# Revit family: Dauphin-Bosse S4_Space Pod_V2
name_source: partatom
category: Casework
units: mm (PartAtom-declared; Revit-internal decimal feet)

## family parameters
Always vertical = Yes
Cut with Voids When Loaded = No
Room Calculation Point = No
Shared = No
Work Plane-Based = No

## types (4) — shared parameters
Dauphin Floor = Bosse_Fabric Divina Asphalt Grey
Dauphin_AC Console = Bosse_Door Metal Material
Dauphin_Glass = Bosse_Panel Glass Material
Dauphin_Handle = Bosse_Door Handle Material
Dauphin_Metal = Bosse_Panel Exterior Material
Dauphin_White = Bosse_Panel Exterior Material
Door Opening Width = 998 mm  [stored 3.27428 ft]
Door Width = 914 mm  [stored 2.99869 ft]
Front Panel Amounts = 3
Height = 2502 mm  [stored 8.20866 ft]
Manufacturer = Dauphin North America
Type Comments = Bosse Series 4

## per-type parameters (varying)
| type | Back Panel Amount | Depth | Description | Floor Width | Froor Depth | Light Visibility | Model | Side Panel Amounts | Width |
| Bosse S4 - Small | 3 | 2514 mm  [stored 8.24803 ft] | Bosse S4 Small PURE | 1996 mm  [stored 6.54856 ft] | 2358 mm  [stored 7.73622 ft] | No | BP4S_P85X99X99 | 3 | 2152 mm  [stored 7.06037 ft] |
| Bosse S4 - Medium | 3 | 2514 mm  [stored 8.24803 ft] | Bosse S4 Mediun PURE | 2358 mm  [stored 7.73622 ft] | 2358 mm  [stored 7.73622 ft] | No | BP4S_P99X99X99 | 3 | 2514 mm  [stored 8.24803 ft] |
| Bosse S4 - Large | 4 | 3149 mm  [stored 10.3314 ft] | Bosse S4 Large PURE | 2993 mm  [stored 9.81955 ft] | 2993 mm  [stored 9.81955 ft] | No | BP4SP124X124X99 | 4 | 3149 mm  [stored 10.3314 ft] |
| Bosse S4 - Extra Large | 4 | 4140 mm  [stored 13.5827 ft] | Bosse S4 Extra Large PURE | 3984 mm | 3984 mm | Yes | BP4SP163X163X99 | 4 | 4140 mm  [stored 13.5827 ft] |

note: [stored X ft] marks values corroborated as IEEE doubles in the binary element streams (Revit-internal decimal feet)

## geometry (parser evidence)
native form markers: Sweep x54
no freeform markers — native parametric forms only
